# Revit family: PPP-NexSentials-ReForm-Waste_Receptacle
name_source: partatom
category: Furniture
revit_build: Autodesk Revit 2014 (Build: 20140709_2115(x64)
units: mm (PartAtom-declared; Revit-internal decimal feet)

## types (3) — shared parameters
Assembly Code = E2020200
Depth = 22"
Doors = PPP Laminate - Graphite 8829-58
Glides = PPP Plastic - Black
Height = 32"
Keynote = 12500
Low Emitting Finish = Yes
Low Emitting Material = Yes
Manufacturer = PPP
Salvage or Reuse = Yes
Series = NexSentials
Type Comments = ReForm
URL = www.peterpepper.com
op 4 = 36 1/2"
zero-valued in all types: Percentage of Recycled Content

## per-type parameters (varying)
| type | 1 Panel | 2 Panel | 4 opn | Description | Model | Open 3 | Open 4 | Width | op 1 | op 2 | op 3 |
| RF24, Waste Rec | Yes | No | No | Waste Receptacle, Top Opening, 24"w x 32"h x 22"d | RF24 | 28" | 28" | 24" | 2 1/2" | 13 1/2" | 25 1/2" |
| RF48, Waste Rec | No | Yes | Yes | Waste Receptacle, Top Opening,  48"w x 32"h x 22"d | RF48 | 31" | 31" | 48" | 3 1/2" | 14 1/2" | 25 1/2" |
| RF36, Waste Rec | No | Yes | No | Waste Receptacle, Top Opening,  36"w x 32"h x 22"d | RF36 | 31" | 28" | 36" | 3" | 14" | 25" |

## geometry (parser evidence)
native form markers: Sweep x4
no freeform markers — native parametric forms only
